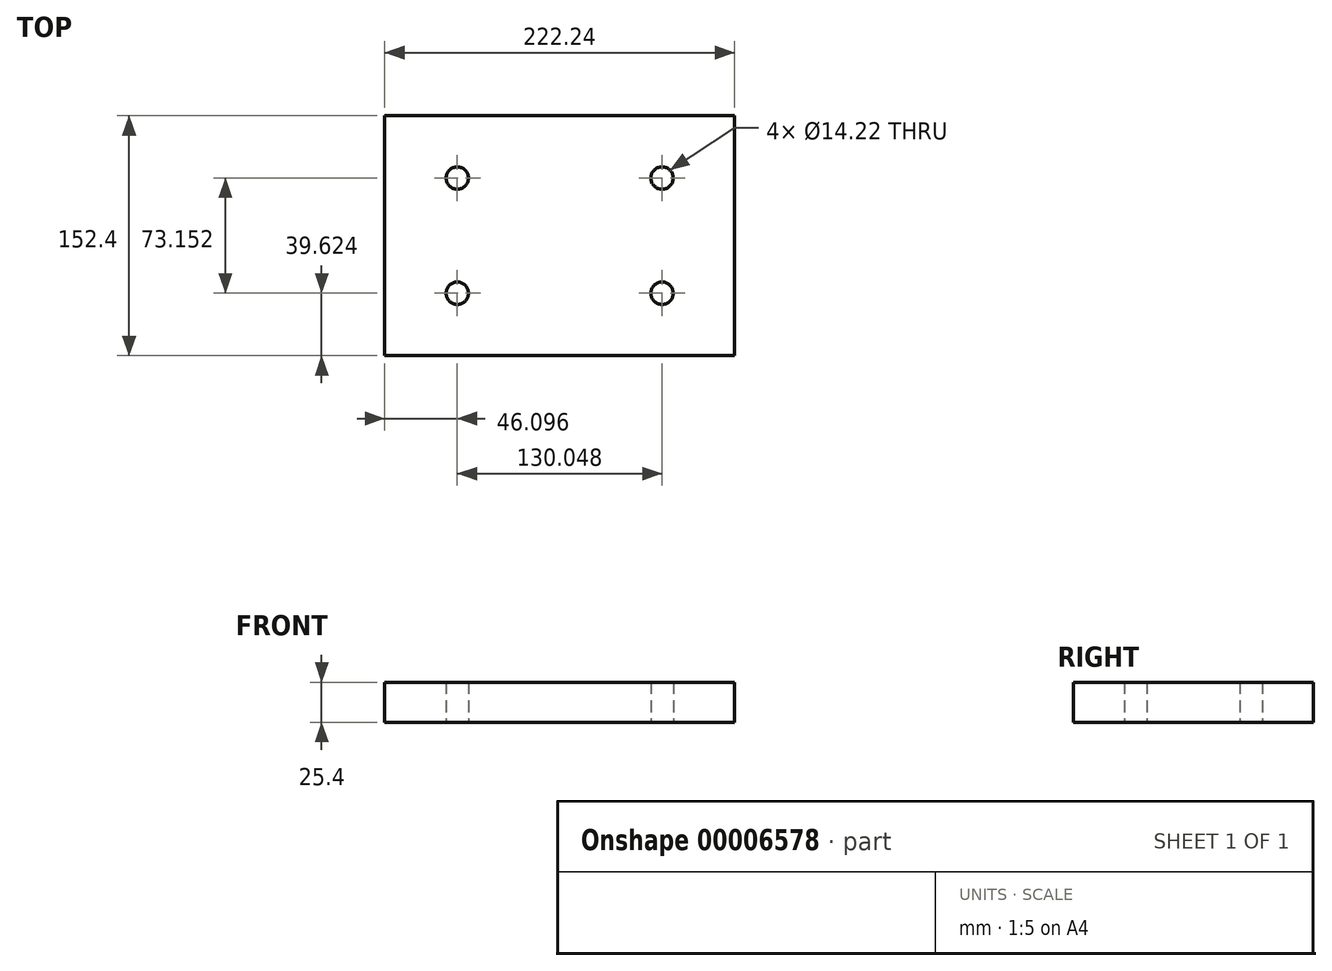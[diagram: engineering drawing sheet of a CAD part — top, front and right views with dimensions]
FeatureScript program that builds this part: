
annotation { "Feature Type Name" : "Feature", "Feature Type Description" : "" }
export const myFeature = defineFeature(function(context is Context, id is Id, definition is map)
    precondition{}
    {
        {
            var Q0;
            Q0=qCreatedBy(makeId("Top.planeOp"),FACE);
            var sketch = newSketch(context, id + "F0", { "sketchPlane" : qUnion([Q0])});
            skLineSegment(sketch, "E0.rect.bottom", {"start": v(-111.13, 76.2) * mm, "end": v(111.13, 76.2) * mm});
            skLineSegment(sketch, "E0.rect.top", {"start": v(-111.13, -76.2) * mm, "end": v(111.13, -76.2) * mm});
            skLineSegment(sketch, "E0.rect.left", {"start": v(-111.13, 76.2) * mm, "end": v(-111.13, -76.2) * mm});
            skLineSegment(sketch, "E0.rect.right", {"start": v(111.13, 76.2) * mm, "end": v(111.13, -76.2) * mm});
            skPoint(sketch, "E0.rect.middle", {"position": v(0, 0) * mm});
            skLineSegment(sketch, "E1.bottom", {"start": v(-111.13, 76.2) * mm, "end": v(0, 76.2) * mm, "construction": true});
            skLineSegment(sketch, "E1.top", {"start": v(-111.13, 0) * mm, "end": v(0, 0) * mm, "construction": true});
            skLineSegment(sketch, "E1.left", {"start": v(-111.13, 76.2) * mm, "end": v(-111.13, 0) * mm, "construction": true});
            skLineSegment(sketch, "E1.right", {"start": v(0, 76.2) * mm, "end": v(0, 0) * mm, "construction": true});
            skLineSegment(sketch, "E2.0", {"start": v(-65.02, 76.2) * mm, "end": v(-65.02, 0) * mm, "construction": true});
            skLineSegment(sketch, "E3.0", {"start": v(-111.13, 36.58) * mm, "end": v(0, 36.58) * mm, "construction": true});
            skCircle(sketch, "E4", {"center": v(-65.02, 36.58) * mm, "radius": 7.11 * mm});
            skCircle(sketch, "E5.0.MirrorC", {"center": v(65.02, 36.58) * mm, "radius": 7.11 * mm});
            skCircle(sketch, "E6.0.MirrorC", {"center": v(-65.02, -36.58) * mm, "radius": 7.11 * mm});
            skCircle(sketch, "E7.0.MirrorC", {"center": v(65.02, -36.58) * mm, "radius": 7.11 * mm});
            skSolve(sketch);
        }
        {
            var Q0;
            Q0=makeQuery(id+"F0.imprint","IMPRINT",FACE,{"disambiguationData":[TD([[makeQuery(id+"F0.imprint","IMPRINT",EDGE,{"derivedFrom":sQuery(id+"F0.wireOp",EDGE,"E0.rect.bottom")}),-1.0]])]});
            extrude(context, id + "F1", {"entities" : qUnion([Q0]), "depth" : 25.4 * mm});
        }
    });
